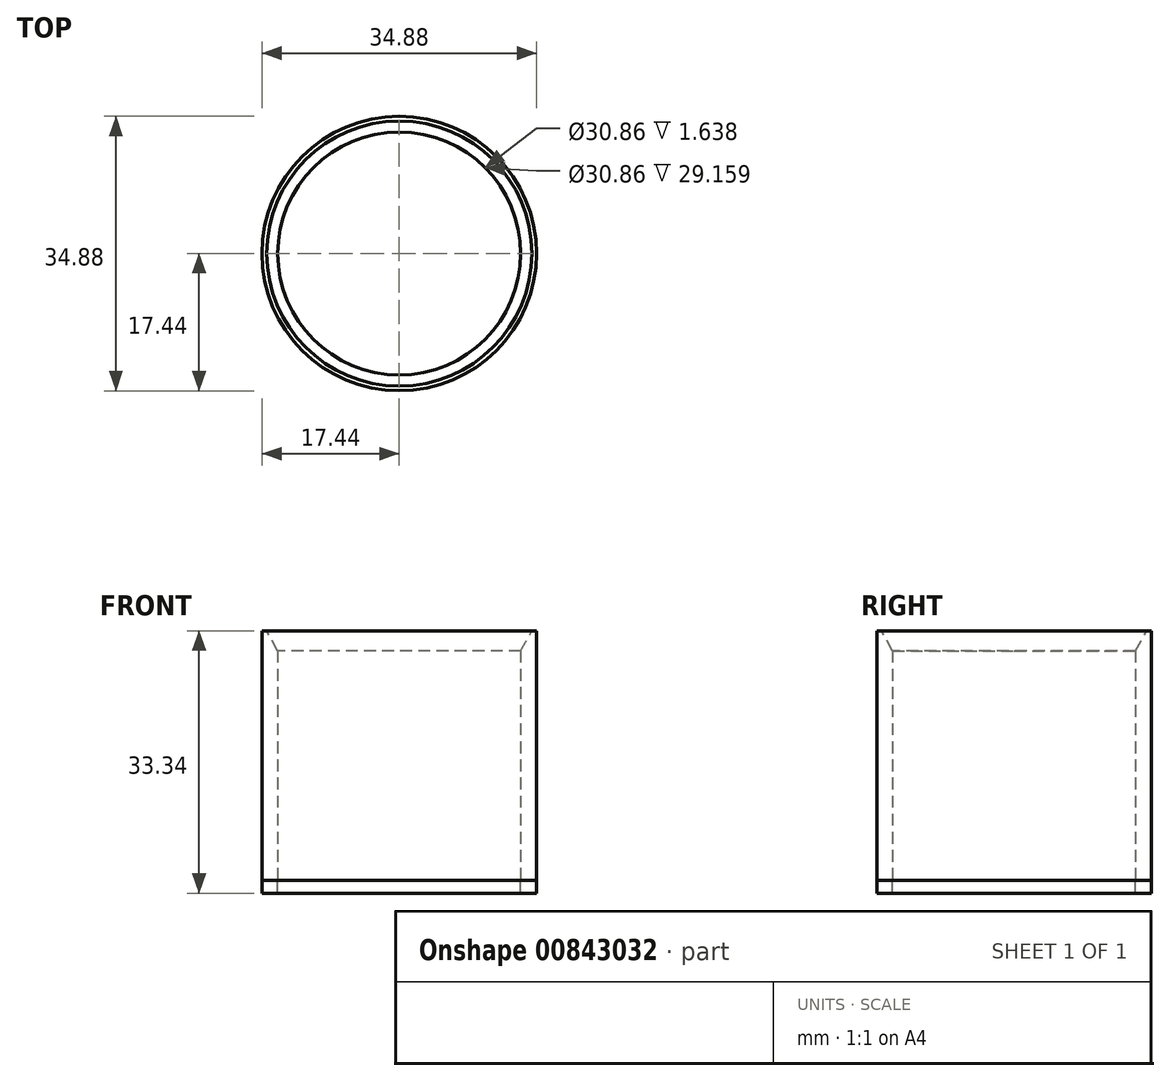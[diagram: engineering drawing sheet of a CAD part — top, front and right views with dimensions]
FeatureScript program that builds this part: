
annotation { "Feature Type Name" : "Feature", "Feature Type Description" : "" }
export const myFeature = defineFeature(function(context is Context, id is Id, definition is map)
    precondition{}
    {
        {
            var Q0;
            Q0=qCreatedBy(makeId("Top.planeOp"),FACE);
            var sketch = newSketch(context, id + "F0", { "sketchPlane" : qUnion([Q0])});
            skLineSegment(sketch, "E0.bottom", {"start": v(42.05, -35.73) * mm, "end": v(-42.05, -35.73) * mm});
            skLineSegment(sketch, "E0.top", {"start": v(42.05, 35.73) * mm, "end": v(-42.05, 35.73) * mm});
            skLineSegment(sketch, "E0.left", {"start": v(42.05, -35.73) * mm, "end": v(42.05, 35.73) * mm});
            skLineSegment(sketch, "E0.right", {"start": v(-42.05, -35.73) * mm, "end": v(-42.05, 35.73) * mm});
            skPoint(sketch, "E0.middle", {"position": v(0, 0) * mm});
            skCircle(sketch, "E1", {"center": v(0, 0) * mm, "radius": 17.44 * mm});
            skCircle(sketch, "E2", {"center": v(0, 0) * mm, "radius": 15.43 * mm});
            skCircle(sketch, "E3", {"center": v(0, 0) * mm, "radius": 16.83 * mm});
            skSolve(sketch);
        }
        {
            var Q0;
            Q0=makeQuery(id+"F0.imprint","IMPRINT",FACE,{"disambiguationData":[TD([[makeQuery(id+"F0.imprint","IMPRINT",EDGE,{"derivedFrom":sQuery(id+"F0.wireOp",EDGE,"E1")}),1.0]])]});
            var Q1;
            Q1=makeQuery(id+"F0.imprint","IMPRINT",FACE,{"disambiguationData":[TD([[makeQuery(id+"F0.imprint","IMPRINT",EDGE,{"derivedFrom":sQuery(id+"F0.wireOp",EDGE,"E2")}),-1.0]])]});
            extrude(context, id + "F1", {"entities" : qUnion([Q0, Q1]), "depth" : 31.7 * mm});
        }
        {
            var Q0;
            Q0=makeQuery(id+"F0.imprint","IMPRINT",FACE,{"disambiguationData":[TD([[makeQuery(id+"F0.imprint","IMPRINT",EDGE,{"derivedFrom":sQuery(id+"F0.wireOp",EDGE,"E1")}),1.0]])]});
            var Q1;
            Q1=makeQuery(id+"F0.imprint","IMPRINT",FACE,{"disambiguationData":[TD([[makeQuery(id+"F0.imprint","IMPRINT",EDGE,{"derivedFrom":sQuery(id+"F0.wireOp",EDGE,"E2")}),-1.0]])]});
            extrude(context, id + "F2", {"entities" : qUnion([Q0, Q1]), "oppositeDirection" : true, "depth" : 1.64 * mm});
        }
        {
            var Q0;
            Q0=makeQuery(id+"F1.opExtrude","CAP_EDGE",EDGE,{"disambiguationData":[OSD([sQuery(id+"F0.wireOp",EDGE,"E2")])],"isStart":false});
            chamfer(context, id + "F3", {"entities" : qUnion([Q0]), "chamferType" : ChamferType.OFFSET_ANGLE, "width" : 2.54 * mm, "oppositeDirection" : false, "angle" : 29 * degree, "tangentPropagation" : true});
        }
    });
